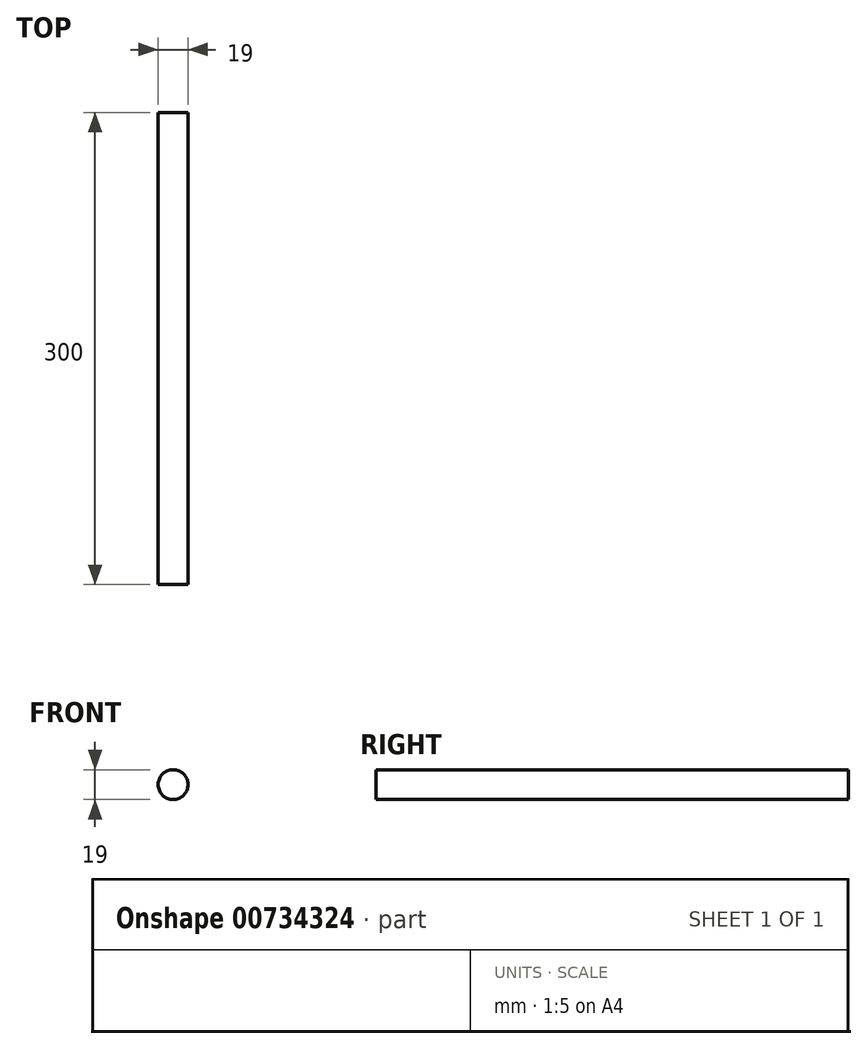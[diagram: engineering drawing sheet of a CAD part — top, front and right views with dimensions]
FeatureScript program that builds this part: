
annotation { "Feature Type Name" : "Feature", "Feature Type Description" : "" }
export const myFeature = defineFeature(function(context is Context, id is Id, definition is map)
    precondition{}
    {
        {
            var Q0;
            Q0=qCreatedBy(makeId("Front.planeOp"),FACE);
            var sketch = newSketch(context, id + "F0", { "sketchPlane" : qUnion([Q0])});
            skCircle(sketch, "E0", {"center": v(0, 0) * mm, "radius": 9.5 * mm});
            skSolve(sketch);
        }
        {
            var Q0;
            Q0 = qSketchRegion(id + "F0", true);
            extrude(context, id + "F1", {"entities" : qUnion([Q0]), "depth" : 300 * mm, "offsetDistance" : 25 * mm});
        }
    });
